# Revit family: 32_Vari-Doors Solide RZ + Berklon stomp
name_source: partatom
category: Doors
units: mm (PartAtom-declared; Revit-internal decimal feet)

## family parameters
Always vertical = Yes
Cut with Voids When Loaded = No
Host = Wall
OmniClass Number = 23.30.10.00
OmniClass Title = Doors
Room Calculation Point = No
Shared = No

## types (1)
- 930X2315
    60_45 Model kozijn = Vari-Doors Solide schuifdeurkozijn
    60_61 Max deurhoogte igv verdiepingshoog = -105 mm
    60_63 Vloerplafondhoogte = 0 mm  [stored 0 ft]
    60_81 Uitvoering kozijn = Kozijn zonder bovenlicht
    60_84 Type kozijn = Vari-Doors Solide schuifdeurkozijn
    70_88 Uitvoering deur = standaard
    70_90 Type deur = Berklon, lakdeur
    80_30 Krukgathoogte = 1050 mm
    80_60 Kantuitvoering = stomp
    80_75 Deurhoogte = 2315 mm  [stored 7.59514 ft]
    80_90 Deurbreedte actieve deur = 930 mm  [stored 3.05118 ft]
    Analytic Construction = <None>
    Assembly Code = 32.32
    Compartmentation = No
    FireExit = No
    Function = Interior
    Height = 0 mm  [stored 0 ft]
    IsExternal = No
    M1 = Berkvens <maak keuze>
    M2 = Berkvens_gebroken wit
    M3 = Berkvens_kristalwit
    M4 = Berkvens_reinwit
    M5 = Berkvens_kristalwit
    M6 = Berkvens_gebroken wit
    Manufacturer = Vari-Doors
    Model = Vari-Doors Solide
    SelfClosing = No
    SmokeStop = No
    URL = www.varidoors.nl
    Versie = 1.0
    Wall Closure = By host
    Width = 0 mm  [stored 0 ft]

note: [stored X ft] marks values corroborated as IEEE doubles in the binary element streams (Revit-internal decimal feet)

## geometry (parser evidence)
native form markers: Sweep x17
no freeform markers — native parametric forms only
